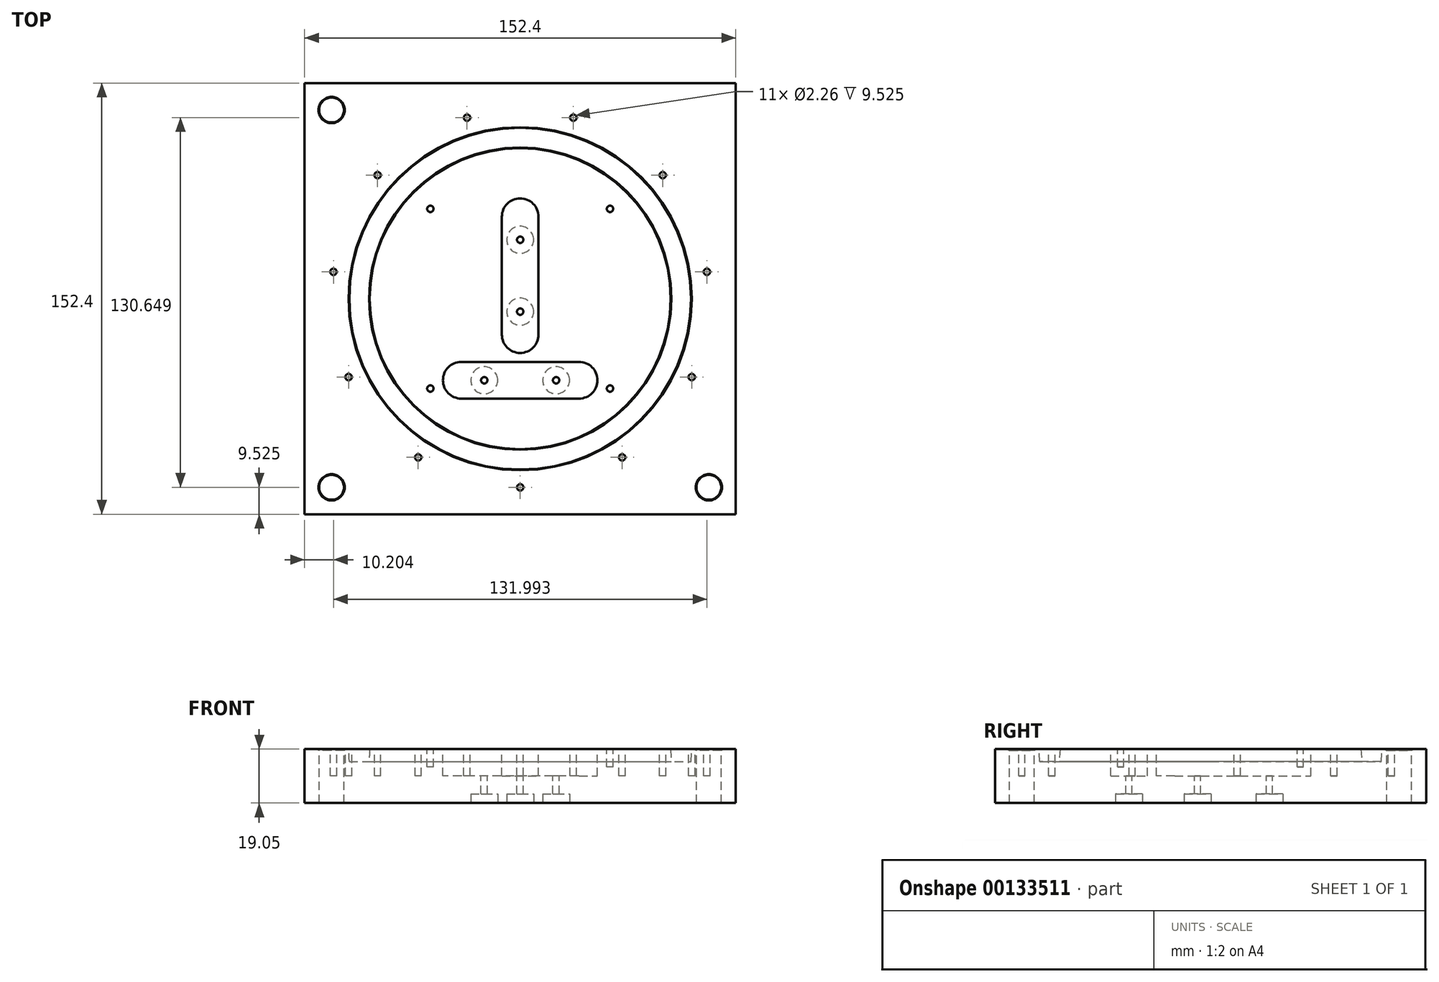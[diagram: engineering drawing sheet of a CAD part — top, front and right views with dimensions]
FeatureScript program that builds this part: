
annotation { "Feature Type Name" : "Feature", "Feature Type Description" : "" }
export const myFeature = defineFeature(function(context is Context, id is Id, definition is map)
    precondition{}
    {
        {
            var Q0;
            Q0=qCreatedBy(makeId("Top.planeOp"),FACE);
            var sketch = newSketch(context, id + "F0", { "sketchPlane" : qUnion([Q0])});
            skLineSegment(sketch, "E0.bottom", {"start": v(76.2, -76.2) * mm, "end": v(-76.2, -76.2) * mm});
            skLineSegment(sketch, "E0.top", {"start": v(76.2, 76.2) * mm, "end": v(-76.2, 76.2) * mm});
            skLineSegment(sketch, "E0.left", {"start": v(76.2, -76.2) * mm, "end": v(76.2, 76.2) * mm});
            skLineSegment(sketch, "E0.right", {"start": v(-76.2, -76.2) * mm, "end": v(-76.2, 76.2) * mm});
            skPoint(sketch, "E0.middle", {"position": v(0, 0) * mm});
            skSolve(sketch);
        }
        {
            var Q0;
            Q0 = qSketchRegion(id + "F0", true);
            extrude(context, id + "F1", {"entities" : qUnion([Q0]), "depth" : 19.05 * mm});
        }
        {
            var Q0;
            Q0=makeQuery(id+"F1.opExtrude","CAP_FACE",FACE,{"disambiguationData":[OSD([sQuery(id+"F0.wireOp",EDGE,"E0.bottom"),sQuery(id+"F0.wireOp",EDGE,"E0.top"),sQuery(id+"F0.wireOp",EDGE,"E0.left"),sQuery(id+"F0.wireOp",EDGE,"E0.right")])],"isStart":false});
            var sketch = newSketch(context, id + "F2", { "sketchPlane" : qUnion([Q0])});
            skCircle(sketch, "E1", {"center": v(-66.67, 66.67) * mm, "radius": 4.38 * mm});
            skCircle(sketch, "E2", {"center": v(-66.67, -66.68) * mm, "radius": 4.38 * mm});
            skCircle(sketch, "E3", {"center": v(66.67, -66.68) * mm, "radius": 4.38 * mm});
            skLineSegment(sketch, "E4", {"start": v(-66.67, -66.68) * mm, "end": v(66.67, -66.68) * mm, "construction": true});
            skSolve(sketch);
        }
        {
            var Q0;
            Q0 = qSketchRegion(id + "F2", true);
            extrude(context, id + "F3", {"entities" : qUnion([Q0]), "operationType" : NewBodyOperationType.REMOVE, "endBound" : BoundingType.UP_TO_NEXT, "oppositeDirection" : true, "depth" : 25.4 * mm});
        }
        {
            var Q0;
            {var subQ0=sQuery(id+"F0.wireOp",EDGE,"E0.right");var subQ1=sQuery(id+"F0.wireOp",EDGE,"E0.left");var subQ2=sQuery(id+"F0.wireOp",EDGE,"E0.top");var subQ3=sQuery(id+"F0.wireOp",EDGE,"E0.bottom");Q0=makeQuery(id+"FHUIdomBf1dPfoC_1.boolean.opBoolean","SPLIT",FACE,{"disambiguationData":[TD([makeQuery(id+"F1.opExtrude","SWEPT_FACE",FACE,{"disambiguationData":[OSD([subQ3])]})])],"derivedFrom":makeQuery(id+"F1.opExtrude","CAP_FACE",FACE,{"disambiguationData":[OSD([subQ3,subQ2,subQ1,subQ0])],"isStart":false})});}
            var sketch = newSketch(context, id + "F4", { "sketchPlane" : qUnion([Q0])});
            skCircle(sketch, "E5", {"center": v(-66.67, 66.67) * mm, "radius": 4.64 * mm});
            skCircle(sketch, "E6", {"center": v(-66.67, -66.68) * mm, "radius": 4.64 * mm});
            skCircle(sketch, "E7", {"center": v(66.67, -66.68) * mm, "radius": 4.64 * mm});
            skSolve(sketch);
        }
        {
            var Q0;
            Q0 = qSketchRegion(id + "F4", true);
            extrude(context, id + "F5", {"entities" : qUnion([Q0]), "operationType" : NewBodyOperationType.REMOVE, "oppositeDirection" : true, "depth" : 0.5 * mm});
        }
        {
            var Q0;
            Q0=makeQuery(id+"F1.opExtrude","CAP_FACE",FACE,{"disambiguationData":[OSD([sQuery(id+"F0.wireOp",EDGE,"E0.bottom"),sQuery(id+"F0.wireOp",EDGE,"E0.top"),sQuery(id+"F0.wireOp",EDGE,"E0.left"),sQuery(id+"F0.wireOp",EDGE,"E0.right")])],"isStart":false});
            var sketch = newSketch(context, id + "F6", { "sketchPlane" : qUnion([Q0])});
            skLineSegment(sketch, "E8.bottom", {"start": v(31.75, -31.75) * mm, "end": v(-31.75, -31.75) * mm, "construction": true});
            skLineSegment(sketch, "E8.top", {"start": v(31.75, 31.75) * mm, "end": v(-31.75, 31.75) * mm, "construction": true});
            skLineSegment(sketch, "E8.left", {"start": v(31.75, -31.75) * mm, "end": v(31.75, 31.75) * mm, "construction": true});
            skLineSegment(sketch, "E8.right", {"start": v(-31.75, -31.75) * mm, "end": v(-31.75, 31.75) * mm, "construction": true});
            skPoint(sketch, "E8.middle", {"position": v(0, 0) * mm});
            skCircle(sketch, "E9", {"center": v(-31.75, 31.75) * mm, "radius": 1.13 * mm});
            skCircle(sketch, "E10", {"center": v(31.75, 31.75) * mm, "radius": 1.13 * mm});
            skCircle(sketch, "E11", {"center": v(31.75, -31.75) * mm, "radius": 1.13 * mm});
            skCircle(sketch, "E12", {"center": v(-31.75, -31.75) * mm, "radius": 1.13 * mm});
            skSolve(sketch);
        }
        {
            var Q0;
            Q0=makeQuery(id+"F1.opExtrude","CAP_FACE",FACE,{"disambiguationData":[OSD([sQuery(id+"F0.wireOp",EDGE,"E0.bottom"),sQuery(id+"F0.wireOp",EDGE,"E0.top"),sQuery(id+"F0.wireOp",EDGE,"E0.left"),sQuery(id+"F0.wireOp",EDGE,"E0.right")])],"isStart":false});
            var sketch = newSketch(context, id + "F7", { "sketchPlane" : qUnion([Q0])});
            skLineSegment(sketch, "E13.bottom", {"start": v(20.83, -22.35) * mm, "end": v(-20.83, -22.35) * mm});
            skLineSegment(sketch, "E13.top", {"start": v(20.83, -35.3) * mm, "end": v(-20.83, -35.3) * mm});
            skLineSegment(sketch, "E13.left", {"start": v(20.83, -22.35) * mm, "end": v(20.83, -35.3) * mm});
            skLineSegment(sketch, "E13.right", {"start": v(-20.83, -22.35) * mm, "end": v(-20.83, -35.3) * mm});
            skPoint(sketch, "E13.middle", {"position": v(0, -28.83) * mm});
            skCircle(sketch, "E14", {"center": v(20.83, -28.83) * mm, "radius": 6.48 * mm});
            skCircle(sketch, "E15", {"center": v(-20.83, -28.83) * mm, "radius": 6.48 * mm});
            skLineSegment(sketch, "E16.bottom", {"start": v(6.48, -12.7) * mm, "end": v(-6.48, -12.7) * mm});
            skLineSegment(sketch, "E16.top", {"start": v(6.48, 28.96) * mm, "end": v(-6.48, 28.96) * mm});
            skLineSegment(sketch, "E16.left", {"start": v(6.48, -12.7) * mm, "end": v(6.48, 28.96) * mm});
            skLineSegment(sketch, "E16.right", {"start": v(-6.48, -12.7) * mm, "end": v(-6.48, 28.96) * mm});
            skPoint(sketch, "E16.middle", {"position": v(0, 8.13) * mm});
            skCircle(sketch, "E17", {"center": v(0, 28.96) * mm, "radius": 6.48 * mm});
            skCircle(sketch, "E18", {"center": v(0, -12.7) * mm, "radius": 6.48 * mm});
            skLineSegment(sketch, "E19", {"start": v(0, 8.13) * mm, "end": v(0, 0) * mm, "construction": true});
            skLineSegment(sketch, "E20", {"start": v(0, 0) * mm, "end": v(0, -28.83) * mm, "construction": true});
            skSolve(sketch);
        }
        {
            var Q0;
            Q0 = qSketchRegion(id + "F6", true);
            extrude(context, id + "F8", {"entities" : qUnion([Q0]), "operationType" : NewBodyOperationType.REMOVE, "oppositeDirection" : true, "depth" : 6.35 * mm});
        }
        {
            var Q0;
            Q0 = qSketchRegion(id + "F7", true);
            extrude(context, id + "F9", {"entities" : qUnion([Q0]), "operationType" : NewBodyOperationType.REMOVE, "oppositeDirection" : true, "depth" : 9.52 * mm});
        }
        {
            var Q0;
            Q0=makeQuery(id+"F1.opExtrude","CAP_FACE",FACE,{"disambiguationData":[OSD([sQuery(id+"F0.wireOp",EDGE,"E0.bottom"),sQuery(id+"F0.wireOp",EDGE,"E0.top"),sQuery(id+"F0.wireOp",EDGE,"E0.left"),sQuery(id+"F0.wireOp",EDGE,"E0.right")])],"isStart":false});
            var sketch = newSketch(context, id + "F10", { "sketchPlane" : qUnion([Q0])});
            skCircle(sketch, "E21", {"center": v(0, -4.57) * mm, "radius": 1.13 * mm});
            skCircle(sketch, "E22", {"center": v(0, 20.83) * mm, "radius": 1.13 * mm});
            skCircle(sketch, "E23", {"center": v(-12.7, -28.83) * mm, "radius": 1.13 * mm});
            skCircle(sketch, "E24", {"center": v(12.7, -28.83) * mm, "radius": 1.13 * mm});
            skLineSegment(sketch, "E25", {"start": v(-6.48, 8.13) * mm, "end": v(6.48, 8.13) * mm, "construction": true});
            skLineSegment(sketch, "E26", {"start": v(0, -4.57) * mm, "end": v(0, 8.13) * mm, "construction": true});
            skLineSegment(sketch, "E27", {"start": v(0, 8.13) * mm, "end": v(0, 20.83) * mm, "construction": true});
            skLineSegment(sketch, "E28", {"start": v(0, -22.35) * mm, "end": v(0, -35.3) * mm, "construction": true});
            skLineSegment(sketch, "E29", {"start": v(0, -28.83) * mm, "end": v(-12.7, -28.83) * mm, "construction": true});
            skLineSegment(sketch, "E30", {"start": v(0, -28.83) * mm, "end": v(12.7, -28.83) * mm, "construction": true});
            skSolve(sketch);
        }
        {
            var Q0;
            Q0 = qSketchRegion(id + "F10", true);
            var Q1;
            Q1=makeQuery(id+"F1.opExtrude","CAP_FACE",FACE,{"disambiguationData":[OSD([sQuery(id+"F0.wireOp",EDGE,"E0.bottom"),sQuery(id+"F0.wireOp",EDGE,"E0.top"),sQuery(id+"F0.wireOp",EDGE,"E0.left"),sQuery(id+"F0.wireOp",EDGE,"E0.right")])],"isStart":true});
            extrude(context, id + "F11", {"entities" : qUnion([Q0]), "operationType" : NewBodyOperationType.REMOVE, "endBound" : BoundingType.UP_TO_SURFACE, "oppositeDirection" : true, "endBoundEntityFace" : qUnion([Q1]), "depth" : 25.4 * mm});
        }
        {
            var Q0;
            Q0=makeQuery(id+"F1.opExtrude","CAP_FACE",FACE,{"disambiguationData":[OSD([sQuery(id+"F0.wireOp",EDGE,"E0.bottom"),sQuery(id+"F0.wireOp",EDGE,"E0.top"),sQuery(id+"F0.wireOp",EDGE,"E0.left"),sQuery(id+"F0.wireOp",EDGE,"E0.right")])],"isStart":true});
            var sketch = newSketch(context, id + "F12", { "sketchPlane" : qUnion([Q0])});
            skCircle(sketch, "E31", {"center": v(-12.7, 28.83) * mm, "radius": 4.76 * mm});
            skCircle(sketch, "E32", {"center": v(12.7, 28.83) * mm, "radius": 4.76 * mm});
            skCircle(sketch, "E33", {"center": v(0, 4.57) * mm, "radius": 4.76 * mm});
            skCircle(sketch, "E34", {"center": v(0, -20.83) * mm, "radius": 4.76 * mm});
            skSolve(sketch);
        }
        {
            var Q0;
            Q0 = qSketchRegion(id + "F12", true);
            extrude(context, id + "F13", {"entities" : qUnion([Q0]), "operationType" : NewBodyOperationType.REMOVE, "oppositeDirection" : true, "depth" : 3.17 * mm});
        }
        {
            var Q0;
            Q0=makeQuery(id+"F4.imprint","IMPRINT",FACE,{"disambiguationData":[TD([[makeQuery(id+"F4.imprint","IMPRINT",EDGE,{"derivedFrom":sQuery(id+"F4.wireOp",EDGE,"E5")}),-1.0]])]});
            var sketch = newSketch(context, id + "F14", { "sketchPlane" : qUnion([Q0])});
            skCircle(sketch, "E35", {"center": v(0, -66.68) * mm, "radius": 1.13 * mm});
            skCircle(sketch, "E36.1.0", {"center": v(36.05, -56.1) * mm, "radius": 1.13 * mm});
            skCircle(sketch, "E36.2.0", {"center": v(60.65, -27.7) * mm, "radius": 1.13 * mm});
            skCircle(sketch, "E36.3.0", {"center": v(66, 9.49) * mm, "radius": 1.13 * mm});
            skCircle(sketch, "E36.4.0", {"center": v(50.39, 43.66) * mm, "radius": 1.13 * mm});
            skCircle(sketch, "E36.5.0", {"center": v(18.78, 63.97) * mm, "radius": 1.13 * mm});
            skCircle(sketch, "E36.6.0", {"center": v(-18.78, 63.97) * mm, "radius": 1.13 * mm});
            skCircle(sketch, "E36.7.0", {"center": v(-50.39, 43.66) * mm, "radius": 1.13 * mm});
            skCircle(sketch, "E36.8.0", {"center": v(-66, 9.49) * mm, "radius": 1.13 * mm});
            skCircle(sketch, "E36.9.0", {"center": v(-60.65, -27.7) * mm, "radius": 1.13 * mm});
            skPoint(sketch, "E36.center", {"position": v(0, 0) * mm});
            skCircle(sketch, "E37.1.10.0", {"center": v(-36.05, -56.1) * mm, "radius": 1.13 * mm});
            skSolve(sketch);
        }
        {
            var Q0;
            Q0 = qSketchRegion(id + "F14", true);
            extrude(context, id + "F15", {"entities" : qUnion([Q0]), "operationType" : NewBodyOperationType.REMOVE, "oppositeDirection" : true, "depth" : 9.52 * mm});
        }
        {
            var Q0;
            Q0=qCreatedBy(makeId("Right.planeOp"),FACE);
            var sketch = newSketch(context, id + "F16", { "sketchPlane" : qUnion([Q0])});
            skLineSegment(sketch, "E38", {"start": v(0, 0) * mm, "end": v(0, 84.4) * mm, "construction": true});
            skSolve(sketch);
        }
        {
            var Q0;
            Q0=qCreatedBy(makeId("Front.planeOp"),FACE);
            var sketch = newSketch(context, id + "F17", { "sketchPlane" : qUnion([Q0])});
            skLineSegment(sketch, "E39", {"start": v(-60.61, 19.05) * mm, "end": v(-53.19, 19.05) * mm});
            skLineSegment(sketch, "E40", {"start": v(-53.19, 19.05) * mm, "end": v(-53.42, 14.63) * mm});
            skLineSegment(sketch, "E41", {"start": v(-53.42, 14.63) * mm, "end": v(-60.38, 14.63) * mm});
            skLineSegment(sketch, "E42", {"start": v(-60.38, 14.63) * mm, "end": v(-60.61, 19.05) * mm});
            skLineSegment(sketch, "E43", {"start": v(-84.1, 0) * mm, "end": v(91.67, 0) * mm, "construction": true});
            skLineSegment(sketch, "E44", {"start": v(0, 0) * mm, "end": v(0, 47.14) * mm, "construction": true});
            skSolve(sketch);
        }
        {
            var Q0;
            Q0 = qSketchRegion(id + "F17", true);
            var Q1;
            Q1=sQuery(id+"F16.wireOp",EDGE,"E38");
            revolve(context, id + "F18", {"operationType" : NewBodyOperationType.REMOVE, "entities" : qUnion([Q0]), "axis" : qUnion([Q1]), "revolveType" : RevolveType.FULL});
        }
    });
